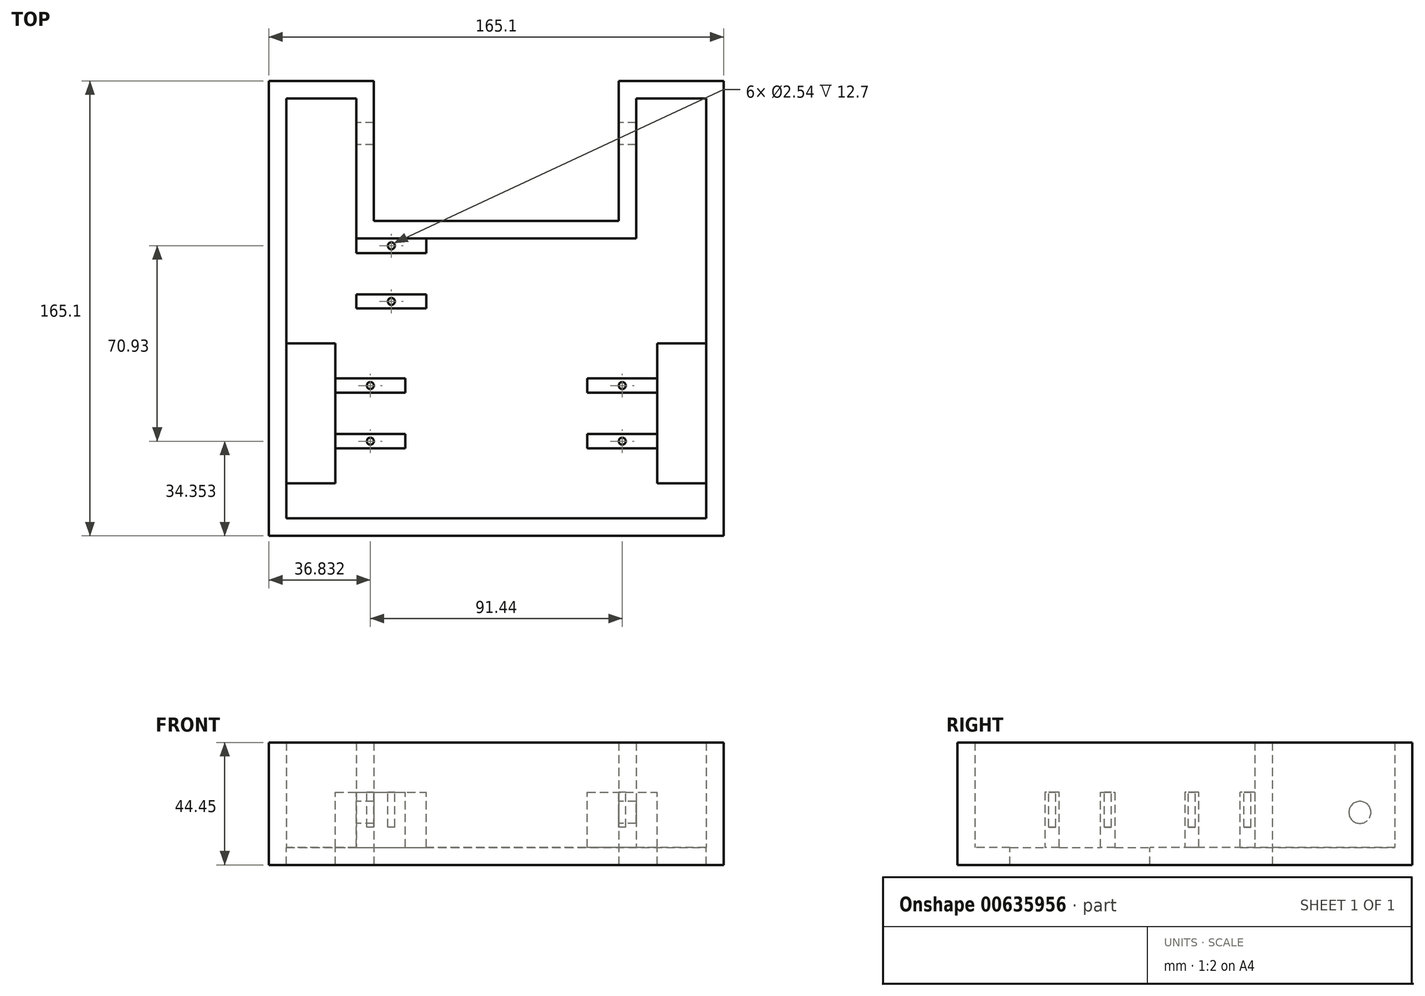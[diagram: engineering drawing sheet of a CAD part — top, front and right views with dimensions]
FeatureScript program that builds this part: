
annotation { "Feature Type Name" : "Feature", "Feature Type Description" : "" }
export const myFeature = defineFeature(function(context is Context, id is Id, definition is map)
    precondition{}
    {
        {
            var Q0;
            Q0=qCreatedBy(makeId("Top.planeOp"),FACE);
            var sketch = newSketch(context, id + "F0", { "sketchPlane" : qUnion([Q0])});
            skLineSegment(sketch, "E0", {"start": v(-89.28, 44.45) * mm, "end": v(-114.68, 44.45) * mm});
            skLineSegment(sketch, "E1", {"start": v(-114.68, 44.45) * mm, "end": v(-114.68, -107.95) * mm});
            skLineSegment(sketch, "E2", {"start": v(-114.68, -107.95) * mm, "end": v(37.72, -107.95) * mm});
            skLineSegment(sketch, "E3", {"start": v(37.72, -107.95) * mm, "end": v(37.72, 44.45) * mm});
            skLineSegment(sketch, "E4", {"start": v(37.72, 44.45) * mm, "end": v(12.32, 44.45) * mm});
            skLineSegment(sketch, "E5", {"start": v(12.32, 44.45) * mm, "end": v(12.32, -6.35) * mm});
            skLineSegment(sketch, "E6", {"start": v(12.32, -6.35) * mm, "end": v(-89.28, -6.35) * mm});
            skLineSegment(sketch, "E7", {"start": v(-89.28, -6.35) * mm, "end": v(-89.28, 44.45) * mm});
            skLineSegment(sketch, "E8", {"start": v(-82.93, 2.7) * mm, "end": v(-82.93, 50.8) * mm});
            skLineSegment(sketch, "E9", {"start": v(-82.93, 50.8) * mm, "end": v(-100.8, 50.8) * mm});
            skLineSegment(sketch, "E10", {"start": v(-100.8, 50.8) * mm, "end": v(-121.03, 50.8) * mm});
            skLineSegment(sketch, "E11", {"start": v(-121.03, 50.8) * mm, "end": v(-121.03, -114.3) * mm});
            skLineSegment(sketch, "E12", {"start": v(-121.03, -114.3) * mm, "end": v(44.07, -114.3) * mm});
            skLineSegment(sketch, "E13", {"start": v(44.07, -114.3) * mm, "end": v(44.07, 50.8) * mm});
            skLineSegment(sketch, "E14", {"start": v(44.07, 50.8) * mm, "end": v(5.97, 50.8) * mm});
            skLineSegment(sketch, "E15", {"start": v(5.97, 50.8) * mm, "end": v(5.97, 0) * mm});
            skLineSegment(sketch, "E16", {"start": v(5.97, 0) * mm, "end": v(-82.93, 0) * mm});
            skLineSegment(sketch, "E17", {"start": v(-82.93, 0) * mm, "end": v(-82.93, 2.7) * mm});
            skSolve(sketch);
        }
        {
            var Q0;
            Q0=makeQuery(id+"F0.imprint","IMPRINT",FACE,{"disambiguationData":[TD([[makeQuery(id+"F0.imprint","IMPRINT",EDGE,{"derivedFrom":sQuery(id+"F0.wireOp",EDGE,"E0")}),-1.0]])]});
            extrude(context, id + "F1", {"entities" : qUnion([Q0]), "depth" : 38.1 * mm, "offsetDistance" : 25.4 * mm});
        }
        {
            var Q0;
            Q0=makeQuery(id+"F1.opExtrude","SWEPT_FACE",FACE,{"disambiguationData":[OSD([sQuery(id+"F0.wireOp",EDGE,"E8"),sQuery(id+"F0.wireOp",EDGE,"E17")])]});
            var sketch = newSketch(context, id + "F2", { "sketchPlane" : qUnion([Q0])});
            skCircle(sketch, "E18", {"center": v(31.75, 12.7) * mm, "radius": 4 * mm});
            skPoint(sketch, "E18.centerSnap0", {"position": v(50.8, 19.05) * mm});
            skPoint(sketch, "E18.centerSnap1", {"position": v(25.4, 0) * mm});
            skSolve(sketch);
        }
        {
            var Q0;
            Q0=makeQuery(id+"F2.imprint","IMPRINT",FACE,{"disambiguationData":[TD([[makeQuery(id+"F2.imprint","IMPRINT",EDGE,{"derivedFrom":sQuery(id+"F2.wireOp",EDGE,"E18")}),1.0]])]});
            extrude(context, id + "F3", {"entities" : qUnion([Q0]), "operationType" : NewBodyOperationType.REMOVE, "depth" : 114.3 * mm, "offsetDistance" : 25.4 * mm, "hasSecondDirection" : true, "secondDirectionOppositeDirection" : true, "secondDirectionDepth" : 6.35 * mm});
        }
        {
            var Q0;
            Q0=makeQuery(id+"F0.imprint","IMPRINT",FACE,{"disambiguationData":[TD([[makeQuery(id+"F0.imprint","IMPRINT",EDGE,{"derivedFrom":sQuery(id+"F0.wireOp",EDGE,"E0")}),1.0]])]});
            var Q1;
            Q1=makeQuery(id+"F0.imprint","IMPRINT",FACE,{"disambiguationData":[TD([[makeQuery(id+"F0.imprint","IMPRINT",EDGE,{"derivedFrom":sQuery(id+"F0.wireOp",EDGE,"E0")}),-1.0]])]});
            extrude(context, id + "F4", {"entities" : qUnion([Q0, Q1]), "operationType" : NewBodyOperationType.ADD, "oppositeDirection" : true, "depth" : 6.35 * mm, "offsetDistance" : 25.4 * mm});
        }
        {
            var Q0;
            {var subQ0=sQuery(id+"F0.wireOp",EDGE,"E15");Q0=makeQuery(id+"F4.boolean.opBoolean","MERGE",FACE,{"derivedFrom":[makeQuery(id+"F1.opExtrude","SWEPT_FACE",FACE,{"disambiguationData":[OSD([subQ0])]}),makeQuery(id+"F4.opExtrude","SWEPT_FACE",FACE,{"disambiguationData":[OSD([subQ0])]})]});}
            var sketch = newSketch(context, id + "F5", { "sketchPlane" : qUnion([Q0])});
            skCircle(sketch, "E19", {"center": v(-31.75, 12.7) * mm, "radius": 4 * mm});
            skPoint(sketch, "E19.centerSnap0", {"position": v(-50.8, 15.88) * mm});
            skPoint(sketch, "E19.centerSnap1", {"position": v(-25.4, -6.35) * mm});
            skSolve(sketch);
        }
        {
            var Q0;
            Q0=makeQuery(id+"F5.imprint","IMPRINT",FACE,{"disambiguationData":[TD([[makeQuery(id+"F5.imprint","IMPRINT",EDGE,{"derivedFrom":sQuery(id+"F5.wireOp",EDGE,"E19")}),1.0]])]});
            extrude(context, id + "F6", {"entities" : qUnion([Q0]), "operationType" : NewBodyOperationType.REMOVE, "oppositeDirection" : true, "depth" : 12.7 * mm, "offsetDistance" : 25.4 * mm});
        }
        {
            var Q0;
            Q0=makeQuery(id+"F4.opExtrude","CAP_FACE",FACE,{"disambiguationData":[OSD([sQuery(id+"F0.wireOp",EDGE,"E8"),sQuery(id+"F0.wireOp",EDGE,"E9"),sQuery(id+"F0.wireOp",EDGE,"E10"),sQuery(id+"F0.wireOp",EDGE,"E11"),sQuery(id+"F0.wireOp",EDGE,"E12"),sQuery(id+"F0.wireOp",EDGE,"E13"),sQuery(id+"F0.wireOp",EDGE,"E14"),sQuery(id+"F0.wireOp",EDGE,"E15"),sQuery(id+"F0.wireOp",EDGE,"E16"),sQuery(id+"F0.wireOp",EDGE,"E17")])],"isStart":true});
            var sketch = newSketch(context, id + "F7", { "sketchPlane" : qUnion([Q0])});
            skLineSegment(sketch, "E20.bottom", {"start": v(-114.68, -95.25) * mm, "end": v(-96.9, -95.25) * mm});
            skLineSegment(sketch, "E20.top", {"start": v(-114.68, -44.45) * mm, "end": v(-96.9, -44.45) * mm});
            skLineSegment(sketch, "E20.right", {"start": v(-96.9, -95.25) * mm, "end": v(-96.9, -44.45) * mm});
            skLineSegment(sketch, "E21", {"start": v(-114.68, -95.25) * mm, "end": v(-114.68, -44.45) * mm});
            skLineSegment(sketch, "E22", {"start": v(37.72, -95.25) * mm, "end": v(19.94, -95.25) * mm});
            skLineSegment(sketch, "E23", {"start": v(19.94, -95.25) * mm, "end": v(19.94, -44.45) * mm});
            skLineSegment(sketch, "E24", {"start": v(19.94, -44.45) * mm, "end": v(37.72, -44.45) * mm});
            skLineSegment(sketch, "E25", {"start": v(37.72, -44.45) * mm, "end": v(37.72, -95.25) * mm});
            skSolve(sketch);
        }
        {
            var Q0;
            Q0=makeQuery(id+"F7.imprint","IMPRINT",FACE,{"disambiguationData":[TD([[makeQuery(id+"F7.imprint","IMPRINT",EDGE,{"derivedFrom":sQuery(id+"F7.wireOp",EDGE,"E20.bottom")}),1.0]])]});
            var Q1;
            Q1=makeQuery(id+"F7.imprint","IMPRINT",FACE,{"disambiguationData":[TD([[makeQuery(id+"F7.imprint","IMPRINT",EDGE,{"derivedFrom":sQuery(id+"F7.wireOp",EDGE,"E22")}),-1.0]])]});
            extrude(context, id + "F8", {"entities" : qUnion([Q0, Q1]), "operationType" : NewBodyOperationType.REMOVE, "oppositeDirection" : true, "depth" : 25.4 * mm, "offsetDistance" : 25.4 * mm});
        }
        {
            var Q0;
            Q0=makeQuery(id+"F4.opExtrude","CAP_FACE",FACE,{"disambiguationData":[OSD([sQuery(id+"F0.wireOp",EDGE,"E8"),sQuery(id+"F0.wireOp",EDGE,"E9"),sQuery(id+"F0.wireOp",EDGE,"E10"),sQuery(id+"F0.wireOp",EDGE,"E11"),sQuery(id+"F0.wireOp",EDGE,"E12"),sQuery(id+"F0.wireOp",EDGE,"E13"),sQuery(id+"F0.wireOp",EDGE,"E14"),sQuery(id+"F0.wireOp",EDGE,"E15"),sQuery(id+"F0.wireOp",EDGE,"E16"),sQuery(id+"F0.wireOp",EDGE,"E17")])],"isStart":true});
            var sketch = newSketch(context, id + "F9", { "sketchPlane" : qUnion([Q0])});
            skLineSegment(sketch, "E26", {"start": v(-96.9, -57.15) * mm, "end": v(19.94, -57.15) * mm});
            skLineSegment(sketch, "E27", {"start": v(19.94, -57.15) * mm, "end": v(19.94, -82.55) * mm});
            skLineSegment(sketch, "E28", {"start": v(19.94, -82.55) * mm, "end": v(-96.9, -82.55) * mm});
            skLineSegment(sketch, "E29", {"start": v(-96.9, -82.55) * mm, "end": v(-96.9, -57.15) * mm});
            skLineSegment(sketch, "E30", {"start": v(-5.46, -57.15) * mm, "end": v(-5.46, -82.55) * mm});
            skLineSegment(sketch, "E31", {"start": v(-71.5, -57.15) * mm, "end": v(-71.5, -82.55) * mm});
            skSolve(sketch);
        }
        {
            var Q0;
            {var subQ0=sQuery(id+"F9.wireOp",EDGE,"E29");Q0=makeQuery(id+"F9.imprint","IMPRINT",FACE,{"disambiguationData":[TD([[makeQuery(id+"F9.imprint","IMPRINT",EDGE,{"derivedFrom":subQ0}),-1.0]])]});}
            var Q1;
            {var subQ0=sQuery(id+"F9.wireOp",EDGE,"E27");Q1=makeQuery(id+"F9.imprint","IMPRINT",FACE,{"disambiguationData":[TD([[makeQuery(id+"F9.imprint","IMPRINT",EDGE,{"derivedFrom":subQ0}),1.0]])]});}
            extrude(context, id + "F10", {"entities" : qUnion([Q0, Q1]), "operationType" : NewBodyOperationType.ADD, "depth" : 20.07 * mm, "offsetDistance" : 25.4 * mm});
        }
        {
            var Q0;
            Q0=makeQuery(id+"F10.opExtrude","CAP_FACE",FACE,{"disambiguationData":[OSD([sQuery(id+"F9.wireOp",EDGE,"E26"),sQuery(id+"F9.wireOp",EDGE,"E28"),sQuery(id+"F9.wireOp",EDGE,"E29"),sQuery(id+"F9.wireOp",EDGE,"E31")])],"isStart":false});
            var sketch = newSketch(context, id + "F11", { "sketchPlane" : qUnion([Q0])});
            skLineSegment(sketch, "E32.bottom", {"start": v(-96.9, -63.5) * mm, "end": v(-71.5, -63.5) * mm});
            skLineSegment(sketch, "E32.top", {"start": v(-96.9, -76.2) * mm, "end": v(-71.5, -76.2) * mm});
            skLineSegment(sketch, "E32.left", {"start": v(-96.9, -63.5) * mm, "end": v(-96.9, -76.2) * mm});
            skLineSegment(sketch, "E32.right", {"start": v(-71.5, -63.5) * mm, "end": v(-71.5, -76.2) * mm});
            skLineSegment(sketch, "E33.bottom", {"start": v(-67, -57.15) * mm, "end": v(-60.66, -57.15) * mm});
            skLineSegment(sketch, "E33.top", {"start": v(-67, -82.55) * mm, "end": v(-60.66, -82.55) * mm});
            skLineSegment(sketch, "E33.left", {"start": v(-67, -57.15) * mm, "end": v(-67, -82.55) * mm});
            skLineSegment(sketch, "E33.right", {"start": v(-60.66, -57.15) * mm, "end": v(-60.66, -82.55) * mm});
            skSolve(sketch);
        }
        {
            var Q0;
            {var subQ0=sQuery(id+"F11.wireOp",EDGE,"E32.left");Q0=makeQuery(id+"F11.imprint","IMPRINT",FACE,{"disambiguationData":[TD([[makeQuery(id+"F11.imprint","IMPRINT",EDGE,{"derivedFrom":subQ0}),-1.0]])]});}
            var Q1;
            {var subQ0=sQuery(id+"F11.wireOp",EDGE,"E32.right");Q1=makeQuery(id+"F11.imprint","IMPRINT",FACE,{"disambiguationData":[TD([[makeQuery(id+"F11.imprint","IMPRINT",EDGE,{"derivedFrom":subQ0}),-1.0]])]});}
            var Q2;
            {var subQ0=sQuery(id+"F11.wireOp",EDGE,"E33.left");var subQ1=sQuery(id+"F11.wireOp",EDGE,"E32.bottom");var subQ2=makeQuery(id+"F11.imprint","INTERSECT",VERTEX,{"derivedFrom":[subQ1,subQ0]});Q2=makeQuery(id+"F11.imprint","IMPRINT",FACE,{"disambiguationData":[TD([[makeQuery(id+"F11.imprint","IMPRINT",EDGE,{"disambiguationData":[TD([[subQ2,-1.0]])],"derivedFrom":subQ1}),-1.0]])]});}
            extrude(context, id + "F12", {"entities" : qUnion([Q0, Q1, Q2]), "operationType" : NewBodyOperationType.REMOVE, "oppositeDirection" : true, "depth" : 19.05 * mm, "offsetDistance" : 25.4 * mm});
        }
        {
            var Q0;
            {var subQ5=sQuery(id+"F11.wireOp",EDGE,"E33.bottom");Q0=makeQuery(id+"F11.imprint","IMPRINT",FACE,{"disambiguationData":[TD([[makeQuery(id+"F11.imprint","IMPRINT",EDGE,{"derivedFrom":subQ5}),-1.0]])]});}
            var Q1;
            {var subQ5=sQuery(id+"F11.wireOp",EDGE,"E33.top");Q1=makeQuery(id+"F11.imprint","IMPRINT",FACE,{"disambiguationData":[TD([[makeQuery(id+"F11.imprint","IMPRINT",EDGE,{"derivedFrom":subQ5}),-1.0]])]});}
            extrude(context, id + "F13", {"entities" : qUnion([Q0, Q1]), "operationType" : NewBodyOperationType.REMOVE, "oppositeDirection" : true, "depth" : 2.54 * mm, "offsetDistance" : 25.4 * mm});
        }
        {
            var Q0;
            Q0=makeQuery(id+"F10.opExtrude","CAP_FACE",FACE,{"disambiguationData":[OSD([sQuery(id+"F9.wireOp",EDGE,"E26"),sQuery(id+"F9.wireOp",EDGE,"E27"),sQuery(id+"F9.wireOp",EDGE,"E28"),sQuery(id+"F9.wireOp",EDGE,"E30")])],"isStart":false});
            var sketch = newSketch(context, id + "F14", { "sketchPlane" : qUnion([Q0])});
            skLineSegment(sketch, "E34", {"start": v(-5.46, -62.36) * mm, "end": v(19.94, -62.36) * mm});
            skLineSegment(sketch, "E35", {"start": v(19.94, -62.36) * mm, "end": v(19.94, -77.34) * mm});
            skLineSegment(sketch, "E36", {"start": v(19.94, -77.34) * mm, "end": v(-5.46, -77.34) * mm});
            skLineSegment(sketch, "E37", {"start": v(-5.46, -77.34) * mm, "end": v(-5.46, -62.36) * mm});
            skLineSegment(sketch, "E38", {"start": v(4.07, -57.15) * mm, "end": v(4.07, -82.55) * mm});
            skLineSegment(sketch, "E39", {"start": v(4.07, -82.55) * mm, "end": v(10.42, -82.55) * mm});
            skLineSegment(sketch, "E40", {"start": v(10.42, -82.55) * mm, "end": v(10.42, -57.15) * mm});
            skLineSegment(sketch, "E41", {"start": v(10.42, -57.15) * mm, "end": v(4.07, -57.15) * mm});
            skSolve(sketch);
        }
        {
            var Q0;
            {var subQ0=sQuery(id+"F14.wireOp",EDGE,"E35");Q0=makeQuery(id+"F14.imprint","IMPRINT",FACE,{"disambiguationData":[TD([[makeQuery(id+"F14.imprint","IMPRINT",EDGE,{"derivedFrom":subQ0}),1.0]])]});}
            var Q1;
            {var subQ0=sQuery(id+"F14.wireOp",EDGE,"E37");Q1=makeQuery(id+"F14.imprint","IMPRINT",FACE,{"disambiguationData":[TD([[makeQuery(id+"F14.imprint","IMPRINT",EDGE,{"derivedFrom":subQ0}),1.0]])]});}
            var Q2;
            {var subQ0=sQuery(id+"F14.wireOp",EDGE,"E38");var subQ1=sQuery(id+"F14.wireOp",EDGE,"E34");var subQ2=makeQuery(id+"F14.imprint","INTERSECT",VERTEX,{"derivedFrom":[subQ1,subQ0]});Q2=makeQuery(id+"F14.imprint","IMPRINT",FACE,{"disambiguationData":[TD([[makeQuery(id+"F14.imprint","IMPRINT",EDGE,{"disambiguationData":[TD([[subQ2,-1.0]])],"derivedFrom":subQ1}),-1.0]])]});}
            extrude(context, id + "F15", {"entities" : qUnion([Q0, Q1, Q2]), "operationType" : NewBodyOperationType.REMOVE, "oppositeDirection" : true, "depth" : 20.07 * mm, "offsetDistance" : 25.4 * mm});
        }
        {
            var Q0;
            Q0=makeQuery(id+"F15.boolean.opBoolean","MERGE",FACE,{"derivedFrom":[makeQuery(id+"F12.boolean.opBoolean","MERGE",FACE,{"derivedFrom":[makeQuery(id+"F4.opExtrude","CAP_FACE",FACE,{"disambiguationData":[OSD([sQuery(id+"F0.wireOp",EDGE,"E8"),sQuery(id+"F0.wireOp",EDGE,"E9"),sQuery(id+"F0.wireOp",EDGE,"E10"),sQuery(id+"F0.wireOp",EDGE,"E11"),sQuery(id+"F0.wireOp",EDGE,"E12"),sQuery(id+"F0.wireOp",EDGE,"E13"),sQuery(id+"F0.wireOp",EDGE,"E14"),sQuery(id+"F0.wireOp",EDGE,"E15"),sQuery(id+"F0.wireOp",EDGE,"E16"),sQuery(id+"F0.wireOp",EDGE,"E17")])],"isStart":true}),makeQuery(id+"F12.opExtrude","CAP_FACE",FACE,{"disambiguationData":[OSD([sQuery(id+"F11.wireOp",EDGE,"E32.bottom"),sQuery(id+"F11.wireOp",EDGE,"E32.top"),sQuery(id+"F11.wireOp",EDGE,"E32.left"),sQuery(id+"F11.wireOp",EDGE,"E32.right")])],"isStart":false})]}),makeQuery(id+"F15.opExtrude","CAP_FACE",FACE,{"disambiguationData":[OSD([sQuery(id+"F9.wireOp",EDGE,"E30"),sQuery(id+"F14.wireOp",EDGE,"511a60dc-ead5-46a0-beed-d69e64ced80c.bottom"),sQuery(id+"F14.wireOp",EDGE,"511a60dc-ead5-46a0-beed-d69e64ced80c.top"),sQuery(id+"F14.wireOp",EDGE,"511a60dc-ead5-46a0-beed-d69e64ced80c.right")])],"isStart":false})]});
            var sketch = newSketch(context, id + "F16", { "sketchPlane" : qUnion([Q0])});
            skLineSegment(sketch, "E42.bottom", {"start": v(-89.28, -6.35) * mm, "end": v(-63.88, -6.35) * mm});
            skLineSegment(sketch, "E42.top", {"start": v(-89.28, -31.75) * mm, "end": v(-63.88, -31.75) * mm});
            skLineSegment(sketch, "E42.left", {"start": v(-89.28, -6.35) * mm, "end": v(-89.28, -31.75) * mm});
            skLineSegment(sketch, "E42.right", {"start": v(-63.88, -6.35) * mm, "end": v(-63.88, -31.75) * mm});
            skSolve(sketch);
        }
        {
            var Q0;
            Q0=makeQuery(id+"F16.imprint","IMPRINT",FACE,{"disambiguationData":[TD([[makeQuery(id+"F16.imprint","IMPRINT",EDGE,{"derivedFrom":sQuery(id+"F16.wireOp",EDGE,"E42.bottom")}),1.0]])]});
            extrude(context, id + "F17", {"entities" : qUnion([Q0]), "operationType" : NewBodyOperationType.ADD, "depth" : 20.07 * mm, "offsetDistance" : 25.4 * mm});
        }
        {
            var Q0;
            Q0=makeQuery(id+"F17.opExtrude","CAP_FACE",FACE,{"disambiguationData":[OSD([sQuery(id+"F16.wireOp",EDGE,"E42.bottom"),sQuery(id+"F16.wireOp",EDGE,"E42.top"),sQuery(id+"F16.wireOp",EDGE,"E42.left"),sQuery(id+"F16.wireOp",EDGE,"E42.right")])],"isStart":false});
            var sketch = newSketch(context, id + "F18", { "sketchPlane" : qUnion([Q0])});
            skLineSegment(sketch, "E43.bottom", {"start": v(-89.3, -12.7) * mm, "end": v(-61.36, -12.7) * mm});
            skLineSegment(sketch, "E43.top", {"start": v(-89.3, -25.4) * mm, "end": v(-61.36, -25.4) * mm});
            skLineSegment(sketch, "E43.left", {"start": v(-89.3, -12.7) * mm, "end": v(-89.3, -25.4) * mm});
            skLineSegment(sketch, "E43.right", {"start": v(-61.36, -12.7) * mm, "end": v(-61.36, -25.4) * mm});
            skLineSegment(sketch, "E44.bottom", {"start": v(-79.73, -6.35) * mm, "end": v(-73.38, -6.35) * mm});
            skLineSegment(sketch, "E44.top", {"start": v(-79.73, -31.75) * mm, "end": v(-73.38, -31.75) * mm});
            skLineSegment(sketch, "E44.left", {"start": v(-79.73, -6.35) * mm, "end": v(-79.73, -31.75) * mm});
            skLineSegment(sketch, "E44.right", {"start": v(-73.38, -6.35) * mm, "end": v(-73.38, -31.75) * mm});
            skSolve(sketch);
        }
        {
            var Q0;
            {var subQ0=sQuery(id+"F18.wireOp",EDGE,"E44.left");var subQ1=sQuery(id+"F18.wireOp",EDGE,"E43.bottom");var subQ2=makeQuery(id+"F18.imprint","INTERSECT",VERTEX,{"derivedFrom":[subQ1,subQ0]});Q0=makeQuery(id+"F18.imprint","IMPRINT",FACE,{"disambiguationData":[TD([[makeQuery(id+"F18.imprint","IMPRINT",EDGE,{"disambiguationData":[TD([[subQ2,1.0]])],"derivedFrom":subQ1}),-1.0]])]});}
            var Q1;
            {var subQ0=sQuery(id+"F18.wireOp",EDGE,"E44.left");var subQ1=sQuery(id+"F18.wireOp",EDGE,"E43.bottom");var subQ2=makeQuery(id+"F18.imprint","INTERSECT",VERTEX,{"derivedFrom":[subQ1,subQ0]});Q1=makeQuery(id+"F18.imprint","IMPRINT",FACE,{"disambiguationData":[TD([[makeQuery(id+"F18.imprint","IMPRINT",EDGE,{"disambiguationData":[TD([[subQ2,-1.0]])],"derivedFrom":subQ1}),-1.0]])]});}
            var Q2;
            {var subQ0=sQuery(id+"F18.wireOp",EDGE,"E43.right");Q2=makeQuery(id+"F18.imprint","IMPRINT",FACE,{"disambiguationData":[TD([[makeQuery(id+"F18.imprint","IMPRINT",EDGE,{"derivedFrom":subQ0}),-1.0]])]});}
            var Q3;
            {var subQ0=sQuery(id+"F18.wireOp",EDGE,"E44.right");var subQ1=sQuery(id+"F18.wireOp",EDGE,"E43.bottom");var subQ2=makeQuery(id+"F18.imprint","INTERSECT",VERTEX,{"derivedFrom":[subQ1,subQ0]});Q3=makeQuery(id+"F18.imprint","IMPRINT",FACE,{"disambiguationData":[TD([[makeQuery(id+"F18.imprint","IMPRINT",EDGE,{"disambiguationData":[TD([[subQ2,-1.0]])],"derivedFrom":subQ1}),-1.0]])]});}
            extrude(context, id + "F19", {"entities" : qUnion([Q0, Q1, Q2, Q3]), "operationType" : NewBodyOperationType.REMOVE, "oppositeDirection" : true, "depth" : 19.05 * mm, "offsetDistance" : 25.4 * mm});
        }
        {
            var Q0;
            {var subQ0=sQuery(id+"F9.wireOp",EDGE,"E29");var subQ1=sQuery(id+"F9.wireOp",EDGE,"E28");var subQ3=sQuery(id+"F9.wireOp",EDGE,"E31");Q0=makeQuery(id+"F12.boolean.opBoolean","SPLIT",FACE,{"disambiguationData":[TD([makeQuery(id+"F12.opExtrude","SWEPT_FACE",FACE,{"disambiguationData":[OSD([sQuery(id+"F11.wireOp",EDGE,"E32.top")])]})])],"derivedFrom":makeQuery(id+"F10.opExtrude","CAP_FACE",FACE,{"disambiguationData":[OSD([sQuery(id+"F9.wireOp",EDGE,"E26"),subQ1,subQ0,subQ3])],"isStart":false})});}
            var sketch = newSketch(context, id + "F20", { "sketchPlane" : qUnion([Q0])});
            skLineSegment(sketch, "E45", {"start": v(-96.9, -62.36) * mm, "end": v(-71.5, -62.36) * mm});
            skLineSegment(sketch, "E46", {"start": v(-71.5, -62.36) * mm, "end": v(-71.5, -77.34) * mm});
            skLineSegment(sketch, "E47", {"start": v(-71.5, -77.34) * mm, "end": v(-96.9, -77.34) * mm});
            skLineSegment(sketch, "E48", {"start": v(-96.9, -77.34) * mm, "end": v(-96.9, -62.36) * mm});
            skLineSegment(sketch, "E49", {"start": v(-87.37, -57.15) * mm, "end": v(-87.37, -82.55) * mm});
            skLineSegment(sketch, "E50", {"start": v(-87.37, -82.55) * mm, "end": v(-81.02, -82.55) * mm});
            skLineSegment(sketch, "E51", {"start": v(-81.02, -82.55) * mm, "end": v(-81.02, -57.15) * mm});
            skLineSegment(sketch, "E52", {"start": v(-81.02, -57.15) * mm, "end": v(-87.37, -57.15) * mm});
            skSolve(sketch);
        }
        {
            var Q0;
            {var subQ0=sQuery(id+"F20.wireOp",EDGE,"E48");var subQ1=sQuery(id+"F20.wireOp",EDGE,"E45");var subQ2=makeQuery(id+"F20.imprint","INTERSECT",VERTEX,{"derivedFrom":[subQ1,subQ0]});Q0=makeQuery(id+"F20.imprint","IMPRINT",FACE,{"disambiguationData":[TD([[makeQuery(id+"F20.imprint","IMPRINT",EDGE,{"disambiguationData":[TD([[subQ2,-1.0]])],"derivedFrom":subQ1}),-1.0]])]});}
            var Q1;
            {var subQ0=sQuery(id+"F20.wireOp",EDGE,"E49");var subQ1=sQuery(id+"F20.wireOp",EDGE,"E45");var subQ2=makeQuery(id+"F20.imprint","INTERSECT",VERTEX,{"derivedFrom":[subQ1,subQ0]});Q1=makeQuery(id+"F20.imprint","IMPRINT",FACE,{"disambiguationData":[TD([[makeQuery(id+"F20.imprint","IMPRINT",EDGE,{"disambiguationData":[TD([[subQ2,-1.0]])],"derivedFrom":subQ1}),-1.0]])]});}
            var Q2;
            {var subQ0=sQuery(id+"F20.wireOp",EDGE,"E46");var subQ1=sQuery(id+"F20.wireOp",EDGE,"E45");var subQ2=makeQuery(id+"F20.imprint","INTERSECT",VERTEX,{"derivedFrom":[subQ1,subQ0]});Q2=makeQuery(id+"F20.imprint","IMPRINT",FACE,{"disambiguationData":[TD([[makeQuery(id+"F20.imprint","IMPRINT",EDGE,{"disambiguationData":[TD([[subQ2,1.0]])],"derivedFrom":subQ1}),-1.0]])]});}
            var Q3;
            {var subQ1=sQuery(id+"F20.wireOp",EDGE,"E47");var subQ8=sQuery(id+"F20.wireOp",EDGE,"E49");var subQ9=makeQuery(id+"F20.imprint","INTERSECT",VERTEX,{"derivedFrom":[subQ1,subQ8]});Q3=makeQuery(id+"F20.imprint","IMPRINT",FACE,{"disambiguationData":[TD([[makeQuery(id+"F20.imprint","IMPRINT",EDGE,{"disambiguationData":[TD([[subQ9,1.0]])],"derivedFrom":subQ8}),-1.0]])]});}
            var Q4;
            {var subQ0=sQuery(id+"F20.wireOp",EDGE,"E51");var subQ1=sQuery(id+"F20.wireOp",EDGE,"E47");var subQ2=makeQuery(id+"F20.imprint","INTERSECT",VERTEX,{"derivedFrom":[subQ1,subQ0]});Q4=makeQuery(id+"F20.imprint","IMPRINT",FACE,{"disambiguationData":[TD([[makeQuery(id+"F20.imprint","IMPRINT",EDGE,{"disambiguationData":[TD([[subQ2,-1.0]])],"derivedFrom":subQ1}),-1.0]])]});}
            var Q5;
            {var subQ4=sQuery(id+"F20.wireOp",EDGE,"E47");var subQ9=sQuery(id+"F20.wireOp",EDGE,"E51");var subQ10=makeQuery(id+"F20.imprint","INTERSECT",VERTEX,{"derivedFrom":[subQ4,subQ9]});Q5=makeQuery(id+"F20.imprint","IMPRINT",FACE,{"disambiguationData":[TD([[makeQuery(id+"F20.imprint","IMPRINT",EDGE,{"disambiguationData":[TD([[subQ10,-1.0]])],"derivedFrom":subQ9}),-1.0]])]});}
            extrude(context, id + "F21", {"entities" : qUnion([Q0, Q1, Q2, Q3, Q4, Q5]), "operationType" : NewBodyOperationType.REMOVE, "oppositeDirection" : true, "depth" : 20.07 * mm, "offsetDistance" : 25.4 * mm});
        }
        {
            var Q0;
            {var subQ3=sQuery(id+"F16.wireOp",EDGE,"E42.top");var subQ4=makeQuery(id+"F17.opExtrude","SWEPT_FACE",FACE,{"disambiguationData":[OSD([subQ3])]});var subQ5=sQuery(id+"F16.wireOp",EDGE,"E42.left");var subQ7=makeQuery(id+"F1.opExtrude","SWEPT_FACE",FACE,{"disambiguationData":[OSD([sQuery(id+"F0.wireOp",EDGE,"E7")])]});var subQ8=sQuery(id+"F16.wireOp",EDGE,"E42.right");Q0=makeQuery(id+"FDOg92NSSSzQfJp_1.boolean.opBoolean","SPLIT",FACE,{"disambiguationData":[TD([subQ7])],"derivedFrom":makeQuery(id+"F19.boolean.opBoolean","SPLIT",FACE,{"disambiguationData":[TD([subQ4])],"derivedFrom":makeQuery(id+"F17.opExtrude","CAP_FACE",FACE,{"disambiguationData":[OSD([sQuery(id+"F16.wireOp",EDGE,"E42.bottom"),subQ3,subQ5,subQ8])],"isStart":false})})});}
            var sketch = newSketch(context, id + "F22", { "sketchPlane" : qUnion([Q0])});
            skLineSegment(sketch, "E53", {"start": v(-89.28, -11.68) * mm, "end": v(-63.88, -11.68) * mm});
            skLineSegment(sketch, "E54", {"start": v(-63.88, -11.68) * mm, "end": v(-63.88, -26.67) * mm});
            skLineSegment(sketch, "E55", {"start": v(-63.88, -26.67) * mm, "end": v(-89.28, -26.67) * mm});
            skLineSegment(sketch, "E56", {"start": v(-89.28, -26.67) * mm, "end": v(-89.28, -11.68) * mm});
            skLineSegment(sketch, "E57", {"start": v(-79.75, -6.48) * mm, "end": v(-79.75, -31.88) * mm});
            skLineSegment(sketch, "E58", {"start": v(-79.75, -31.88) * mm, "end": v(-73.4, -31.88) * mm});
            skLineSegment(sketch, "E59", {"start": v(-73.4, -31.88) * mm, "end": v(-73.4, -6.48) * mm});
            skLineSegment(sketch, "E60", {"start": v(-73.4, -6.48) * mm, "end": v(-79.75, -6.48) * mm});
            skSolve(sketch);
        }
        {
            var Q0;
            {var subQ0=sQuery(id+"F22.wireOp",EDGE,"E56");var subQ1=sQuery(id+"F22.wireOp",EDGE,"E53");var subQ2=makeQuery(id+"F22.imprint","INTERSECT",VERTEX,{"derivedFrom":[subQ1,subQ0]});Q0=makeQuery(id+"F22.imprint","IMPRINT",FACE,{"disambiguationData":[TD([[makeQuery(id+"F22.imprint","IMPRINT",EDGE,{"disambiguationData":[TD([[subQ2,-1.0]])],"derivedFrom":subQ1}),-1.0]])]});}
            var Q1;
            {var subQ1=sQuery(id+"F22.wireOp",EDGE,"E53");var subQ11=sQuery(id+"F22.wireOp",EDGE,"E57");var subQ12=makeQuery(id+"F22.imprint","INTERSECT",VERTEX,{"derivedFrom":[subQ1,subQ11]});Q1=makeQuery(id+"F22.imprint","IMPRINT",FACE,{"disambiguationData":[TD([[makeQuery(id+"F22.imprint","IMPRINT",EDGE,{"disambiguationData":[TD([[subQ12,-1.0]])],"derivedFrom":subQ1}),-1.0]])]});}
            var Q2;
            {var subQ0=sQuery(id+"F22.wireOp",EDGE,"E54");Q2=makeQuery(id+"F22.imprint","IMPRINT",FACE,{"disambiguationData":[TD([[makeQuery(id+"F22.imprint","IMPRINT",EDGE,{"derivedFrom":subQ0}),-1.0]])]});}
            var Q3;
            {var subQ1=sQuery(id+"F22.wireOp",EDGE,"E55");var subQ10=sQuery(id+"F22.wireOp",EDGE,"E57");var subQ11=makeQuery(id+"F22.imprint","INTERSECT",VERTEX,{"derivedFrom":[subQ1,subQ10]});Q3=makeQuery(id+"F22.imprint","IMPRINT",FACE,{"disambiguationData":[TD([[makeQuery(id+"F22.imprint","IMPRINT",EDGE,{"disambiguationData":[TD([[subQ11,-1.0]])],"derivedFrom":subQ1}),-1.0]])]});}
            var Q4;
            {var subQ0=sQuery(id+"F22.wireOp",EDGE,"E57");var subQ1=sQuery(id+"F22.wireOp",EDGE,"E55");var subQ2=makeQuery(id+"F22.imprint","INTERSECT",VERTEX,{"derivedFrom":[subQ1,subQ0]});Q4=makeQuery(id+"F22.imprint","IMPRINT",FACE,{"disambiguationData":[TD([[makeQuery(id+"F22.imprint","IMPRINT",EDGE,{"disambiguationData":[TD([[subQ2,1.0]])],"derivedFrom":subQ1}),-1.0]])]});}
            extrude(context, id + "F23", {"entities" : qUnion([Q0, Q1, Q2, Q3, Q4]), "operationType" : NewBodyOperationType.REMOVE, "oppositeDirection" : true, "depth" : 20.07 * mm, "offsetDistance" : 25.4 * mm});
        }
        {
            var Q0;
            {var subQ0=sQuery(id+"F9.wireOp",EDGE,"E29");var subQ1=sQuery(id+"F9.wireOp",EDGE,"E28");var subQ3=sQuery(id+"F9.wireOp",EDGE,"E31");Q0=makeQuery(id+"F12.boolean.opBoolean","SPLIT",FACE,{"disambiguationData":[TD([makeQuery(id+"F12.opExtrude","SWEPT_FACE",FACE,{"disambiguationData":[OSD([sQuery(id+"F11.wireOp",EDGE,"E32.top")])]})])],"derivedFrom":makeQuery(id+"F10.opExtrude","CAP_FACE",FACE,{"disambiguationData":[OSD([sQuery(id+"F9.wireOp",EDGE,"E26"),subQ1,subQ0,subQ3])],"isStart":false})});}
            var sketch = newSketch(context, id + "F24", { "sketchPlane" : qUnion([Q0])});
            skCircle(sketch, "E61", {"center": v(-84.2, -79.95) * mm, "radius": 1.27 * mm});
            skPoint(sketch, "E61.centerSnap0", {"position": v(-71.5, -79.95) * mm});
            skPoint(sketch, "E61.centerSnap1", {"position": v(-84.2, -82.55) * mm});
            skSolve(sketch);
        }
        {
            var Q0;
            {var subQ0=sQuery(id+"F9.wireOp",EDGE,"E29");var subQ1=sQuery(id+"F9.wireOp",EDGE,"E26");var subQ3=sQuery(id+"F9.wireOp",EDGE,"E31");Q0=makeQuery(id+"F12.boolean.opBoolean","SPLIT",FACE,{"disambiguationData":[TD([makeQuery(id+"F12.opExtrude","SWEPT_FACE",FACE,{"disambiguationData":[OSD([sQuery(id+"F11.wireOp",EDGE,"E32.bottom")])]})])],"derivedFrom":makeQuery(id+"F10.opExtrude","CAP_FACE",FACE,{"disambiguationData":[OSD([subQ1,sQuery(id+"F9.wireOp",EDGE,"E28"),subQ0,subQ3])],"isStart":false})});}
            var sketch = newSketch(context, id + "F25", { "sketchPlane" : qUnion([Q0])});
            skCircle(sketch, "E62", {"center": v(-84.2, -59.75) * mm, "radius": 1.27 * mm});
            skSolve(sketch);
        }
        {
            var Q0;
            {var subQ0=sQuery(id+"F16.wireOp",EDGE,"E42.right");var subQ1=sQuery(id+"F16.wireOp",EDGE,"E42.top");var subQ2=sQuery(id+"F16.wireOp",EDGE,"E42.left");Q0=makeQuery(id+"F19.boolean.opBoolean","SPLIT",FACE,{"disambiguationData":[TD([makeQuery(id+"F17.opExtrude","SWEPT_FACE",FACE,{"disambiguationData":[OSD([subQ1])]})])],"derivedFrom":makeQuery(id+"F17.opExtrude","CAP_FACE",FACE,{"disambiguationData":[OSD([sQuery(id+"F16.wireOp",EDGE,"E42.bottom"),subQ1,subQ2,subQ0])],"isStart":false})});}
            var sketch = newSketch(context, id + "F26", { "sketchPlane" : qUnion([Q0])});
            skCircle(sketch, "E63", {"center": v(-76.58, -29.21) * mm, "radius": 1.27 * mm});
            skSolve(sketch);
        }
        {
            var Q0;
            {var subQ0=sQuery(id+"F16.wireOp",EDGE,"E42.right");var subQ1=sQuery(id+"F16.wireOp",EDGE,"E42.left");Q0=makeQuery(id+"F19.boolean.opBoolean","SPLIT",FACE,{"disambiguationData":[TD([makeQuery(id+"F1.opExtrude","SWEPT_FACE",FACE,{"disambiguationData":[OSD([sQuery(id+"F0.wireOp",EDGE,"E6")])]})])],"derivedFrom":makeQuery(id+"F17.opExtrude","CAP_FACE",FACE,{"disambiguationData":[OSD([sQuery(id+"F16.wireOp",EDGE,"E42.bottom"),sQuery(id+"F16.wireOp",EDGE,"E42.top"),subQ1,subQ0])],"isStart":false})});}
            var sketch = newSketch(context, id + "F27", { "sketchPlane" : qUnion([Q0])});
            skCircle(sketch, "E64", {"center": v(-76.58, -9.02) * mm, "radius": 1.27 * mm});
            skSolve(sketch);
        }
        {
            var Q0;
            {var subQ0=sQuery(id+"F9.wireOp",EDGE,"E30");var subQ1=sQuery(id+"F9.wireOp",EDGE,"E28");var subQ2=sQuery(id+"F9.wireOp",EDGE,"E27");Q0=makeQuery(id+"F15.boolean.opBoolean","SPLIT",FACE,{"disambiguationData":[TD([makeQuery(id+"F15.opExtrude","SWEPT_FACE",FACE,{"disambiguationData":[OSD([sQuery(id+"F14.wireOp",EDGE,"E36")])]})])],"derivedFrom":makeQuery(id+"F10.opExtrude","CAP_FACE",FACE,{"disambiguationData":[OSD([sQuery(id+"F9.wireOp",EDGE,"E26"),subQ2,subQ1,subQ0])],"isStart":false})});}
            var sketch = newSketch(context, id + "F28", { "sketchPlane" : qUnion([Q0])});
            skCircle(sketch, "E65", {"center": v(7.24, -79.95) * mm, "radius": 1.27 * mm});
            skSolve(sketch);
        }
        {
            var Q0;
            {var subQ0=sQuery(id+"F9.wireOp",EDGE,"E30");var subQ1=sQuery(id+"F9.wireOp",EDGE,"E27");var subQ2=sQuery(id+"F9.wireOp",EDGE,"E26");Q0=makeQuery(id+"F15.boolean.opBoolean","SPLIT",FACE,{"disambiguationData":[TD([makeQuery(id+"F15.opExtrude","SWEPT_FACE",FACE,{"disambiguationData":[OSD([sQuery(id+"F14.wireOp",EDGE,"E34")])]})])],"derivedFrom":makeQuery(id+"F10.opExtrude","CAP_FACE",FACE,{"disambiguationData":[OSD([subQ2,subQ1,sQuery(id+"F9.wireOp",EDGE,"E28"),subQ0])],"isStart":false})});}
            var sketch = newSketch(context, id + "F29", { "sketchPlane" : qUnion([Q0])});
            skCircle(sketch, "E66", {"center": v(7.24, -59.75) * mm, "radius": 1.27 * mm});
            skSolve(sketch);
        }
        {
            var Q0;
            Q0=makeQuery(id+"F29.imprint","IMPRINT",FACE,{"disambiguationData":[TD([[makeQuery(id+"F29.imprint","IMPRINT",EDGE,{"derivedFrom":sQuery(id+"F29.wireOp",EDGE,"E66")}),1.0]])]});
            var Q1;
            Q1=makeQuery(id+"F28.imprint","IMPRINT",FACE,{"disambiguationData":[TD([[makeQuery(id+"F28.imprint","IMPRINT",EDGE,{"derivedFrom":sQuery(id+"F28.wireOp",EDGE,"E65")}),1.0]])]});
            var Q2;
            Q2=makeQuery(id+"F24.imprint","IMPRINT",FACE,{"disambiguationData":[TD([[makeQuery(id+"F24.imprint","IMPRINT",EDGE,{"derivedFrom":sQuery(id+"F24.wireOp",EDGE,"E61")}),1.0]])]});
            var Q3;
            Q3=makeQuery(id+"F25.imprint","IMPRINT",FACE,{"disambiguationData":[TD([[makeQuery(id+"F25.imprint","IMPRINT",EDGE,{"derivedFrom":sQuery(id+"F25.wireOp",EDGE,"E62")}),1.0]])]});
            var Q4;
            Q4=makeQuery(id+"F26.imprint","IMPRINT",FACE,{"disambiguationData":[TD([[makeQuery(id+"F26.imprint","IMPRINT",EDGE,{"derivedFrom":sQuery(id+"F26.wireOp",EDGE,"E63")}),1.0]])]});
            var Q5;
            Q5=makeQuery(id+"F27.imprint","IMPRINT",FACE,{"disambiguationData":[TD([[makeQuery(id+"F27.imprint","IMPRINT",EDGE,{"derivedFrom":sQuery(id+"F27.wireOp",EDGE,"E64")}),1.0]])]});
            extrude(context, id + "F30", {"entities" : qUnion([Q0, Q1, Q2, Q3, Q4, Q5]), "operationType" : NewBodyOperationType.REMOVE, "oppositeDirection" : true, "depth" : 12.7 * mm, "offsetDistance" : 25.4 * mm});
        }
    });
